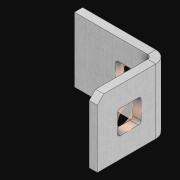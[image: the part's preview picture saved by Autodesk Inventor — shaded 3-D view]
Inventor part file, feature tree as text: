
AUTODESK INVENTOR PART (.ipt)
format: ipt  version: 2021 (Build 250183000, 183)  size: 1,012,736 bytes
history: native  units: in
note: dims shown in document units (in); Inventor stores cm internally (conversion verified against a paired STEP export)
features: extrude x4, sketch x4, pattern_linear x2, other x2, sheet_metal_op x1
ambient origin geometry x8: Origin, YZ Plane, XZ Plane, XY Plane, X Axis, Y Axis, Z Axis, Center Point
bodies: Solid1 (feature_tree)
feature tree (13):
  pattern_linear  "Rectangular Pattern1"  Spacing1=0.5in  [1 undecoded]
  pattern_linear  "Rectangular Pattern3"  Spacing1=0.3937in  [1 undecoded]
  extrude  "Extrusion1"  Depth=0.5in
  extrude  "Extrusion2"  Depth=0.5in
  sketch  "Sketch1"  dims[d0=0.182in]
  other  "Srf1"
  sketch  "Sketch3"  dims[d1=0.063in d2=0.0in]
  other  "Srf3"
  sketch  "Sketch4"  dims[d6=0.182in]
  sketch  "Sketch5"  dims[d7=0.063in d8=0.0in d11=0.5in d12=0.3937in d14=0.5in d18=0.3937in d20=0.5in d21=17.0in d22=0.0in d23=0.841in d24=0.0in]
  sheet_metal_op  "Fold1"
  extrude  "ExtrusionSrf1"  TaperAngle=0.0deg  [1 undecoded]
  extrude  "ExtrusionSrf3"  Depth=0.5in TaperAngle=0.0deg
note: 3 required parameter values undecoded (feature->parameter linkage not recoverable at this tier; creation-order binding heuristic only, values carry confidence <= 0.55)
